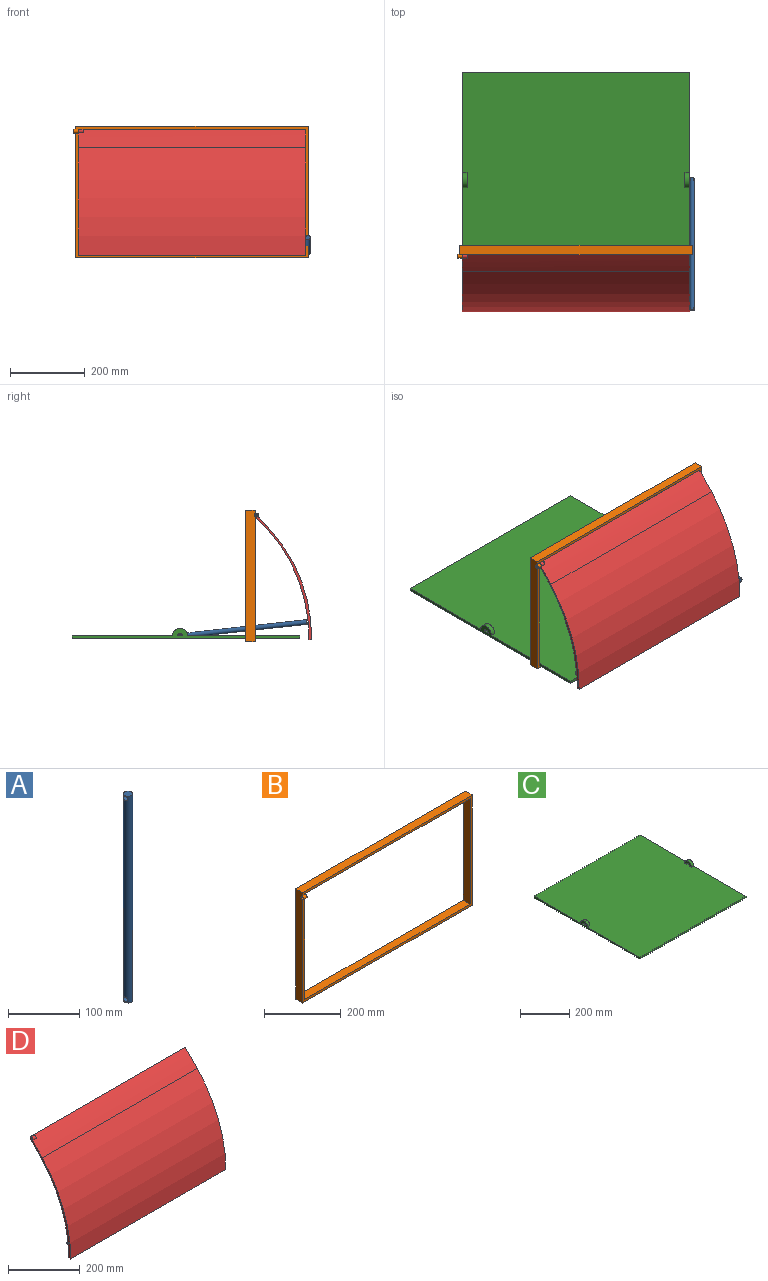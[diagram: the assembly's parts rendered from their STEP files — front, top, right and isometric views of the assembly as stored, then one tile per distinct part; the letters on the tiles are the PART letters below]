
ASSEMBLY  parts=4 mates=5
PART A: 5 faces, bbox 12.7x12.7x355.6 mm
  f0: cylinder r=6.35mm len=355.6mm, axis (0,0,-1), area 13995.8mm2, adj f1,f2,f3,f4
  f1: plane 12.7x12.7mm, normal (0,0,1), area 126.7mm2, adj f0
  f2: plane 12.7x12.7mm, normal (0,0,-1), area 126.7mm2, adj f0
  f3: cylinder r=3.81mm len=12.7mm, axis (1,0,0), area 274.5mm2, adj f0
  f4: cylinder r=3.81mm len=12.7mm, axis (1,0,0), area 274.5mm2, adj f0
PART B: 15 faces, bbox 629.9x34.1x352 mm
  f0: plane 2.59x0.23mm, normal (-1,0,0), area 0.4mm2, adj f1,f13
  f1: plane 7.62x2.59mm, normal (0,-1,0), area 19.8mm2, adj f0,f3,f13
  f2: plane 609.6x25.4mm, normal (0,0,1), area 15483.8mm2, adj f3,f9,f10,f11
  f3: plane 336.8x34.06mm, normal (1,0,0), area 8583.3mm2, adj f1,f2,f4,f10,f11,f12,f13
  f4: plane 609.6x25.4mm, normal (0,0,-1), area 15483.8mm2, adj f3,f9,f10,f11
  f5: plane 624.84x25.4mm, normal (0,0,1), area 15870.9mm2, adj f6,f8,f10,f11
  f6: plane 352.04x25.4mm, normal (-1,0,0), area 8934.5mm2, adj f5,f7,f10,f11,f12
  f7: plane 624.84x25.4mm, normal (0,0,-1), area 15870.9mm2, adj f6,f8,f10,f11
  f8: plane 352.04x25.4mm, normal (1,0,0), area 8941.9mm2, adj f5,f7,f10,f11
  f9: plane 336.8x25.4mm, normal (-1,0,0), area 8554.8mm2, adj f2,f4,f10,f11
  f10: plane 624.84x352.04mm, normal (0,-1,0), area 14600.6mm2, adj f2,f3,f4,f5,f6,f7,f8,f9
  f11: plane 624.84x352.04mm, normal (0,1,0), area 14655.5mm2, adj f2,f3,f4,f5,f6,f7,f8,f9
  f12: cylinder r=5.08mm len=12.7mm, axis (1,0,0), area 344.4mm2, adj f3,f6,f10,f14
  f13: cylinder r=3.81mm len=12.7mm, axis (1,0,0), area 283.9mm2, adj f0,f1,f3,f14
  f14: plane 10.16x10.16mm, normal (-1,0,0), area 35.5mm2, adj f12,f13
PART C: 12 faces, bbox 609.6x609.6x27.9 mm
  f0: plane 609.6x7.62mm, normal (0,1,0), area 4645.2mm2, adj f1,f3,f4,f5
  f1: plane 609.6x27.94mm, normal (-1,0,0), area 5202.5mm2, adj f0,f2,f4,f5,f9,f10
  f2: plane 609.6x7.62mm, normal (0,-1,0), area 4645.2mm2, adj f1,f3,f4,f5
  f3: plane 609.6x27.94mm, normal (1,0,0), area 5202.5mm2, adj f0,f2,f4,f5,f6,f7
  f4: plane 609.6x609.6mm, normal (0,0,1), area 370967mm2, adj f0,f1,f2,f3,f6,f7,f8,f9
  f5: plane 609.6x609.6mm, normal (0,0,-1), area 371612.2mm2, adj f0,f1,f2,f3
  f6: cylinder r=20.32mm len=40.64mm, axis (1,0,0), area 810.7mm2, adj f3,f4,f8
  f7: cylinder r=7.62mm len=15.24mm, axis (1,0,0), area 304mm2, adj f3,f4,f8
  f8: plane 40.64x20.32mm, normal (-1,0,0), area 557.4mm2, adj f4,f6,f7
  f9: cylinder r=20.32mm len=40.64mm, axis (-1,0,0), area 810.7mm2, adj f1,f4,f11
  f10: cylinder r=7.62mm len=15.24mm, axis (-1,0,0), area 304mm2, adj f1,f4,f11
  f11: plane 40.64x20.32mm, normal (1,0,0), area 557.4mm2, adj f4,f9,f10
PART D: 16 faces, bbox 609.6x160x336.8 mm
  f0: cylinder r=893.88mm len=609.6mm, axis (-1,0,0), area 41364.3mm2, adj f2,f3,f4,f5,f13,f14,f15
  f1: plane 609.6x7.62mm, normal (0,0,-1), area 4645.2mm2, adj f3,f4,f5,f6
  f2: plane 609.6x7.62mm, normal (0,1,0), area 4645.2mm2, adj f0,f3,f5,f6
  f3: plane 336.8x160.02mm, normal (-1,0,0), area 2395.6mm2, adj f0,f1,f2,f4,f6,f10,f11,f13
  f4: cylinder r=426.93mm len=609.6mm, axis (-1,0,0), area 193143.4mm2, adj f0,f1,f3,f5
  f5: plane 336.8x160.02mm, normal (1,0,0), area 2376.5mm2, adj f0,f1,f2,f4,f6,f7,f8
  f6: cylinder r=431.72mm len=609.6mm, axis (1,0,0), area 228151.7mm2, adj f1,f2,f3,f5,f7,f8,f9,f10
  f7: cylinder r=5.08mm len=12.7mm, axis (1,0,0), area 201.9mm2, adj f5,f6,f9
  f8: cylinder r=3.81mm len=12.7mm, axis (1,0,0), area 151.6mm2, adj f5,f6,f9
  f9: plane 10.13x5.62mm, normal (-1,0,0), area 17.7mm2, adj f6,f7,f8
  f10: cylinder r=5.08mm len=12.7mm, axis (-1,0,0), area 201.9mm2, adj f3,f6,f12
  f11: cylinder r=3.81mm len=12.7mm, axis (-1,0,0), area 151.6mm2, adj f3,f6,f12
  f12: plane 10.13x5.62mm, normal (1,0,0), area 17.7mm2, adj f6,f10,f11
  f13: cylinder r=3.81mm len=12.7mm, axis (-1,0,0), area 165.2mm2, adj f0,f3,f15
  f14: cylinder r=5.08mm len=12.7mm, axis (-1,0,0), area 216mm2, adj f0,f3,f15
  f15: plane 9.1x8.95mm, normal (1,0,0), area 19.1mm2, adj f0,f13,f14
PLACE A rot(axis=(1,0,0),83.7deg) t=(752.63,-168.57,549.19)mm
PLACE B t=(136.6,-349.64,542.13)mm fixed
PLACE C t=(136.6,115.18,542.13)mm
PLACE D rot(axis=(1,0,0),1.1deg) t=(136.6,-366.4,542.3)mm
MATE revolute C.f6 <-> A.f4  axis (1,0,0) through (746.2,-173.62,549.75)mm
MATE revolute B.f12 <-> D.f13  axis (1,0,0) through (136.6,-378.62,873.85)mm
MATE planar C.f3 <-> B.f9  axis (1,0,0) through (746.2,-187.9,547.36)mm
MATE planar B.f2 <-> C.f5  axis (0,0,1) through (441.4,-362.34,542.13)mm
MATE revolute A.f3 <-> D.f7  axis (1,0,0) through (746.2,-516.98,587.54)mm
